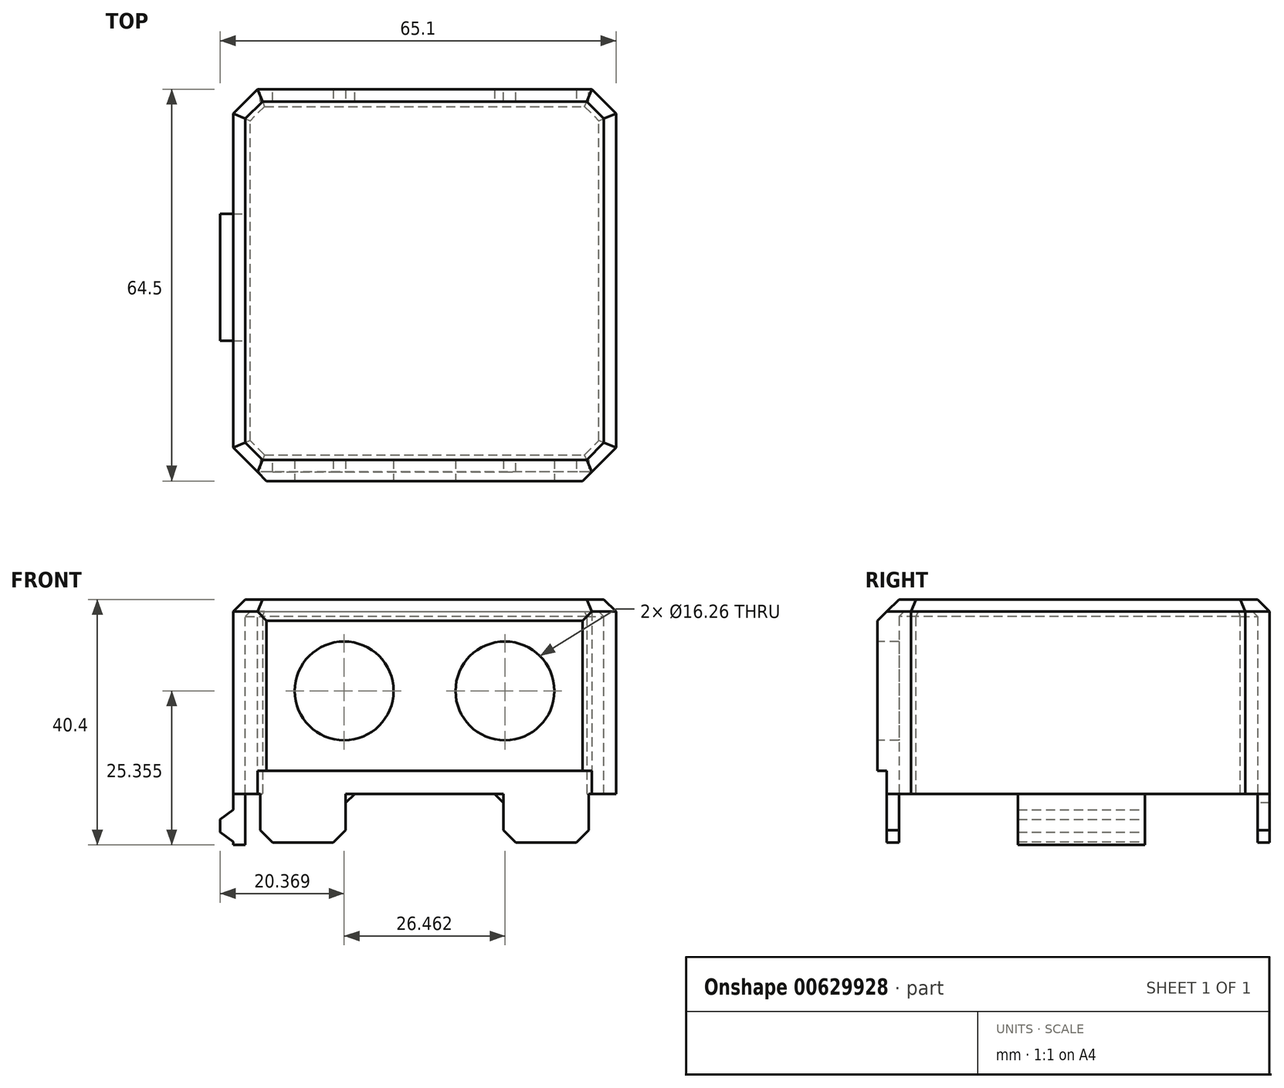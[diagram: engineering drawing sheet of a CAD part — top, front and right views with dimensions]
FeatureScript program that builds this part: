
annotation { "Feature Type Name" : "Feature", "Feature Type Description" : "" }
export const myFeature = defineFeature(function(context is Context, id is Id, definition is map)
    precondition{}
    {
        {
            var Q0;
            Q0=qCreatedBy(makeId("Top.planeOp"),FACE);
            var sketch = newSketch(context, id + "F0", { "sketchPlane" : qUnion([Q0])});
            skLineSegment(sketch, "E0.bottom", {"start": v(0, 0) * mm, "end": v(63, 0) * mm});
            skLineSegment(sketch, "E0.top", {"start": v(0, 63) * mm, "end": v(63, 63) * mm});
            skLineSegment(sketch, "E0.left", {"start": v(0, 0) * mm, "end": v(0, 63) * mm});
            skLineSegment(sketch, "E0.right", {"start": v(63, 0) * mm, "end": v(63, 63) * mm});
            skSolve(sketch);
        }
        {
            var Q0;
            Q0=makeQuery(id+"F0.imprint","IMPRINT",FACE,{"disambiguationData":[TD([[makeQuery(id+"F0.imprint","IMPRINT",EDGE,{"derivedFrom":sQuery(id+"F0.wireOp",EDGE,"E0.bottom")}),1.0]])]});
            extrude(context, id + "F1", {"entities" : qUnion([Q0]), "depth" : 32 * mm, "offsetDistance" : 25 * mm});
        }
        {
            var Q0;
            Q0=makeQuery(id+"F1.opExtrude","SWEPT_EDGE",EDGE,{"disambiguationData":[OSD([sQuery(id+"F0.wireOp",EDGE,"E0.bottom"),sQuery(id+"F0.wireOp",EDGE,"E0.right")])]});
            var Q1;
            Q1=makeQuery(id+"F1.opExtrude","SWEPT_EDGE",EDGE,{"disambiguationData":[OSD([sQuery(id+"F0.wireOp",EDGE,"E0.top"),sQuery(id+"F0.wireOp",EDGE,"E0.right")])]});
            var Q2;
            Q2=makeQuery(id+"F1.opExtrude","SWEPT_EDGE",EDGE,{"disambiguationData":[OSD([sQuery(id+"F0.wireOp",EDGE,"E0.bottom"),sQuery(id+"F0.wireOp",EDGE,"E0.left")])]});
            var Q3;
            Q3=makeQuery(id+"F1.opExtrude","SWEPT_EDGE",EDGE,{"disambiguationData":[OSD([sQuery(id+"F0.wireOp",EDGE,"E0.top"),sQuery(id+"F0.wireOp",EDGE,"E0.left")])]});
            chamfer(context, id + "F2", {"entities" : qUnion([Q0, Q1, Q2, Q3]), "width" : 4 * mm, "tangentPropagation" : true});
        }
        {
            var Q0;
            Q0=makeQuery(id+"F1.opExtrude","CAP_FACE",FACE,{"disambiguationData":[OSD([sQuery(id+"F0.wireOp",EDGE,"E0.bottom"),sQuery(id+"F0.wireOp",EDGE,"E0.top"),sQuery(id+"F0.wireOp",EDGE,"E0.left"),sQuery(id+"F0.wireOp",EDGE,"E0.right")])],"isStart":false});
            chamfer(context, id + "F3", {"entities" : qUnion([Q0]), "width" : 2 * mm, "tangentPropagation" : true});
        }
        {
            var Q0;
            Q0=makeQuery(id+"F1.opExtrude","CAP_FACE",FACE,{"disambiguationData":[OSD([sQuery(id+"F0.wireOp",EDGE,"E0.bottom"),sQuery(id+"F0.wireOp",EDGE,"E0.top"),sQuery(id+"F0.wireOp",EDGE,"E0.left"),sQuery(id+"F0.wireOp",EDGE,"E0.right")])],"isStart":true});
            shell(context, id + "F4", {"entities" : qUnion([Q0]), "thickness" : 2 * mm});
        }
        {
            var Q0;
            Q0=makeQuery(id+"F1.opExtrude","SWEPT_FACE",FACE,{"disambiguationData":[OSD([sQuery(id+"F0.wireOp",EDGE,"E0.bottom")])]});
            var sketch = newSketch(context, id + "F5", { "sketchPlane" : qUnion([Q0])});
            skLineSegment(sketch, "E1.bottom", {"start": v(59, 30) * mm, "end": v(4, 30) * mm});
            skLineSegment(sketch, "E1.top", {"start": v(59, 3.8) * mm, "end": v(4, 3.8) * mm});
            skLineSegment(sketch, "E1.left", {"start": v(59, 30) * mm, "end": v(59, 3.8) * mm});
            skLineSegment(sketch, "E1.right", {"start": v(4, 30) * mm, "end": v(4, 3.8) * mm});
            skSolve(sketch);
        }
        {
            var Q0;
            Q0=makeQuery(id+"F5.imprint","IMPRINT",FACE,{"disambiguationData":[TD([[makeQuery(id+"F5.imprint","IMPRINT",EDGE,{"derivedFrom":sQuery(id+"F5.wireOp",EDGE,"E1.bottom")}),1.0]])]});
            extrude(context, id + "F6", {"entities" : qUnion([Q0]), "operationType" : NewBodyOperationType.ADD, "depth" : 1.5 * mm, "offsetDistance" : 25 * mm});
        }
        {
            var Q0;
            Q0=makeQuery(id+"F6.opExtrude","CAP_EDGE",EDGE,{"disambiguationData":[OSD([sQuery(id+"F5.wireOp",EDGE,"E1.bottom")])],"isStart":false});
            var Q1;
            Q1=makeQuery(id+"F6.opExtrude","CAP_EDGE",EDGE,{"disambiguationData":[OSD([sQuery(id+"F5.wireOp",EDGE,"E1.right")])],"isStart":false});
            var Q2;
            Q2=makeQuery(id+"F6.opExtrude","CAP_EDGE",EDGE,{"disambiguationData":[OSD([sQuery(id+"F5.wireOp",EDGE,"E1.left")])],"isStart":false});
            chamfer(context, id + "F7", {"entities" : qUnion([Q0, Q1, Q2]), "width" : 1.5 * mm, "tangentPropagation" : true});
        }
        {
            var Q0;
            Q0=makeQuery(id+"F6.opExtrude","CAP_FACE",FACE,{"disambiguationData":[OSD([sQuery(id+"F5.wireOp",EDGE,"E1.bottom"),sQuery(id+"F5.wireOp",EDGE,"E1.top"),sQuery(id+"F5.wireOp",EDGE,"E1.left"),sQuery(id+"F5.wireOp",EDGE,"E1.right")])],"isStart":false});
            var sketch = newSketch(context, id + "F8", { "sketchPlane" : qUnion([Q0])});
            skCircle(sketch, "E2", {"center": v(18.27, 16.95) * mm, "radius": 8.13 * mm});
            skCircle(sketch, "E3", {"center": v(44.73, 16.95) * mm, "radius": 8.13 * mm});
            skSolve(sketch);
        }
        {
            var Q0;
            Q0=makeQuery(id+"F8.imprint","IMPRINT",FACE,{"disambiguationData":[TD([[makeQuery(id+"F8.imprint","IMPRINT",EDGE,{"derivedFrom":sQuery(id+"F8.wireOp",EDGE,"E2")}),1.0]])]});
            var Q1;
            Q1=makeQuery(id+"F8.imprint","IMPRINT",FACE,{"disambiguationData":[TD([[makeQuery(id+"F8.imprint","IMPRINT",EDGE,{"derivedFrom":sQuery(id+"F8.wireOp",EDGE,"E3")}),1.0]])]});
            var Q2;
            {var subQ0=sQuery(id+"F0.wireOp",EDGE,"E0.bottom");Q2=makeQuery(id+"F4.opShell","OFFSET_FACE",FACE,{"disambiguationData":[OSD([subQ0]),TDD([makeQuery(id+"F1.opExtrude","SWEPT_FACE",FACE,{"disambiguationData":[OSD([subQ0])]})])]});}
            extrude(context, id + "F9", {"entities" : qUnion([Q0, Q1]), "operationType" : NewBodyOperationType.REMOVE, "endBound" : BoundingType.UP_TO_SURFACE, "oppositeDirection" : true, "depth" : 25 * mm, "endBoundEntityFace" : qUnion([Q2]), "offsetDistance" : 25 * mm});
        }
        {
            var Q0;
            Q0=makeQuery(id+"F1.opExtrude","SWEPT_FACE",FACE,{"disambiguationData":[OSD([sQuery(id+"F0.wireOp",EDGE,"E0.bottom")])]});
            var sketch = newSketch(context, id + "F10", { "sketchPlane" : qUnion([Q0])});
            skLineSegment(sketch, "E4.bottom", {"start": v(4.5, 0) * mm, "end": v(18.5, 0) * mm});
            skLineSegment(sketch, "E4.top", {"start": v(4.5, -8) * mm, "end": v(18.5, -8) * mm});
            skLineSegment(sketch, "E4.left", {"start": v(4.5, 0) * mm, "end": v(4.5, -8) * mm});
            skLineSegment(sketch, "E4.right", {"start": v(18.5, 0) * mm, "end": v(18.5, -8) * mm});
            skLineSegment(sketch, "E5.bottom", {"start": v(58.5, 0) * mm, "end": v(44.5, 0) * mm});
            skLineSegment(sketch, "E5.top", {"start": v(58.5, -8) * mm, "end": v(44.5, -8) * mm});
            skLineSegment(sketch, "E5.left", {"start": v(58.5, 0) * mm, "end": v(58.5, -8) * mm});
            skLineSegment(sketch, "E5.right", {"start": v(44.5, 0) * mm, "end": v(44.5, -8) * mm});
            skSolve(sketch);
        }
        {
            var Q0;
            Q0=makeQuery(id+"F10.imprint","IMPRINT",FACE,{"disambiguationData":[TD([[makeQuery(id+"F10.imprint","IMPRINT",EDGE,{"derivedFrom":sQuery(id+"F10.wireOp",EDGE,"E4.bottom")}),-1.0]])]});
            var Q1;
            Q1=makeQuery(id+"F10.imprint","IMPRINT",FACE,{"disambiguationData":[TD([[makeQuery(id+"F10.imprint","IMPRINT",EDGE,{"derivedFrom":sQuery(id+"F10.wireOp",EDGE,"E5.bottom")}),-1.0]])]});
            var Q2;
            {var subQ0=sQuery(id+"F0.wireOp",EDGE,"E0.bottom");Q2=makeQuery(id+"F4.opShell","OFFSET_FACE",FACE,{"disambiguationData":[OSD([subQ0]),TDD([makeQuery(id+"F1.opExtrude","SWEPT_FACE",FACE,{"disambiguationData":[OSD([subQ0])]})])]});}
            extrude(context, id + "F11", {"entities" : qUnion([Q0, Q1]), "operationType" : NewBodyOperationType.ADD, "endBound" : BoundingType.UP_TO_SURFACE, "oppositeDirection" : true, "depth" : 25 * mm, "endBoundEntityFace" : qUnion([Q2]), "offsetDistance" : 25 * mm});
        }
        {
            var Q0;
            Q0=makeQuery(id+"F1.opExtrude","SWEPT_FACE",FACE,{"disambiguationData":[OSD([sQuery(id+"F0.wireOp",EDGE,"E0.top")])]});
            var Q1;
            Q1=makeQuery(id+"F11.boolean.opBoolean","MERGE",FACE,{"derivedFrom":[makeQuery(id+"F1.opExtrude","SWEPT_FACE",FACE,{"disambiguationData":[OSD([sQuery(id+"F0.wireOp",EDGE,"E0.bottom")])]}),makeQuery(id+"F11.opExtrude","CAP_FACE",FACE,{"disambiguationData":[OSD([sQuery(id+"F10.wireOp",EDGE,"E4.bottom"),sQuery(id+"F10.wireOp",EDGE,"E4.top"),sQuery(id+"F10.wireOp",EDGE,"E4.left"),sQuery(id+"F10.wireOp",EDGE,"E4.right")])],"isStart":true})]});
            cPlane(context, id + "F12", {"entities" : qUnion([Q0, Q1]), "cplaneType" : CPlaneType.MID_PLANE, "offset" : 25 * mm, "width" : 150 * mm, "height" : 150 * mm});
        }
        {
            var Q0;
            Q0=makeQuery(id+"F1.opExtrude","SWEPT_FACE",FACE,{"disambiguationData":[OSD([sQuery(id+"F0.wireOp",EDGE,"E0.top")])]});
            var sketch = newSketch(context, id + "F13", { "sketchPlane" : qUnion([Q0])});
            skLineSegment(sketch, "E6.bottom", {"start": v(-4.5, 0) * mm, "end": v(-18.5, 0) * mm});
            skLineSegment(sketch, "E6.top", {"start": v(-4.5, -8) * mm, "end": v(-18.5, -8) * mm});
            skLineSegment(sketch, "E6.left", {"start": v(-4.5, 0) * mm, "end": v(-4.5, -8) * mm});
            skLineSegment(sketch, "E6.right", {"start": v(-18.5, 0) * mm, "end": v(-18.5, -8) * mm});
            skLineSegment(sketch, "E7.bottom", {"start": v(-58.5, 0) * mm, "end": v(-44.5, 0) * mm});
            skLineSegment(sketch, "E7.top", {"start": v(-58.5, -8) * mm, "end": v(-44.5, -8) * mm});
            skLineSegment(sketch, "E7.left", {"start": v(-58.5, 0) * mm, "end": v(-58.5, -8) * mm});
            skLineSegment(sketch, "E7.right", {"start": v(-44.5, 0) * mm, "end": v(-44.5, -8) * mm});
            skSolve(sketch);
        }
        {
            var Q0;
            Q0=makeQuery(id+"F13.imprint","IMPRINT",FACE,{"disambiguationData":[TD([[makeQuery(id+"F13.imprint","IMPRINT",EDGE,{"derivedFrom":sQuery(id+"F13.wireOp",EDGE,"E7.bottom")}),1.0]])]});
            var Q1;
            Q1=makeQuery(id+"F13.imprint","IMPRINT",FACE,{"disambiguationData":[TD([[makeQuery(id+"F13.imprint","IMPRINT",EDGE,{"derivedFrom":sQuery(id+"F13.wireOp",EDGE,"E6.bottom")}),1.0]])]});
            extrude(context, id + "F14", {"entities" : qUnion([Q0, Q1]), "operationType" : NewBodyOperationType.ADD, "oppositeDirection" : true, "depth" : 2 * mm, "offsetDistance" : 25 * mm});
        }
        {
            var Q0;
            Q0=makeQuery(id+"F11.opExtrude","SWEPT_EDGE",EDGE,{"disambiguationData":[OSD([sQuery(id+"F10.wireOp",EDGE,"E4.top"),sQuery(id+"F10.wireOp",EDGE,"E4.left")])]});
            var Q1;
            Q1=makeQuery(id+"F11.opExtrude","SWEPT_EDGE",EDGE,{"disambiguationData":[OSD([sQuery(id+"F10.wireOp",EDGE,"E4.top"),sQuery(id+"F10.wireOp",EDGE,"E4.right")])]});
            var Q2;
            Q2=makeQuery(id+"F11.opExtrude","SWEPT_EDGE",EDGE,{"disambiguationData":[OSD([sQuery(id+"F10.wireOp",EDGE,"E5.top"),sQuery(id+"F10.wireOp",EDGE,"E5.right")])]});
            var Q3;
            Q3=makeQuery(id+"F11.opExtrude","SWEPT_EDGE",EDGE,{"disambiguationData":[OSD([sQuery(id+"F10.wireOp",EDGE,"E5.top"),sQuery(id+"F10.wireOp",EDGE,"E5.left")])]});
            var Q4;
            Q4=makeQuery(id+"F14.opExtrude","SWEPT_EDGE",EDGE,{"disambiguationData":[OSD([sQuery(id+"F13.wireOp",EDGE,"E6.top"),sQuery(id+"F13.wireOp",EDGE,"E6.right")])]});
            var Q5;
            Q5=makeQuery(id+"F14.opExtrude","SWEPT_EDGE",EDGE,{"disambiguationData":[OSD([sQuery(id+"F13.wireOp",EDGE,"E6.top"),sQuery(id+"F13.wireOp",EDGE,"E6.left")])]});
            var Q6;
            Q6=makeQuery(id+"F14.opExtrude","SWEPT_EDGE",EDGE,{"disambiguationData":[OSD([sQuery(id+"F13.wireOp",EDGE,"E7.top"),sQuery(id+"F13.wireOp",EDGE,"E7.left")])]});
            var Q7;
            Q7=makeQuery(id+"F14.opExtrude","SWEPT_EDGE",EDGE,{"disambiguationData":[OSD([sQuery(id+"F13.wireOp",EDGE,"E7.top"),sQuery(id+"F13.wireOp",EDGE,"E7.right")])]});
            chamfer(context, id + "F15", {"entities" : qUnion([Q0, Q1, Q2, Q3, Q4, Q5, Q6, Q7]), "width" : 2 * mm, "tangentPropagation" : true});
        }
        {
            var Q0;
            Q0=makeQuery(id+"F14.opExtrude","SWEPT_EDGE",EDGE,{"disambiguationData":[OSD([sQuery(id+"F0.wireOp",EDGE,"E0.top"),sQuery(id+"F13.wireOp",EDGE,"E6.bottom"),sQuery(id+"F13.wireOp",EDGE,"E6.right")])]});
            var Q1;
            Q1=makeQuery(id+"F11.opExtrude","SWEPT_EDGE",EDGE,{"disambiguationData":[OSD([sQuery(id+"F0.wireOp",EDGE,"E0.bottom"),sQuery(id+"F10.wireOp",EDGE,"E4.bottom"),sQuery(id+"F10.wireOp",EDGE,"E4.right")])]});
            var Q2;
            Q2=makeQuery(id+"F11.opExtrude","SWEPT_EDGE",EDGE,{"disambiguationData":[OSD([sQuery(id+"F0.wireOp",EDGE,"E0.bottom"),sQuery(id+"F10.wireOp",EDGE,"E5.bottom"),sQuery(id+"F10.wireOp",EDGE,"E5.right")])]});
            var Q3;
            Q3=makeQuery(id+"F14.opExtrude","SWEPT_EDGE",EDGE,{"disambiguationData":[OSD([sQuery(id+"F0.wireOp",EDGE,"E0.top"),sQuery(id+"F13.wireOp",EDGE,"E7.bottom"),sQuery(id+"F13.wireOp",EDGE,"E7.right")])]});
            chamfer(context, id + "F16", {"entities" : qUnion([Q0, Q1, Q2, Q3]), "width" : 1.5 * mm, "tangentPropagation" : true});
        }
        {
            var Q0;
            Q0=qCreatedBy(id+"F12.planeOp",FACE);
            var sketch = newSketch(context, id + "F17", { "sketchPlane" : qUnion([Q0])});
            skLineSegment(sketch, "E8.bottom", {"start": v(0, 0) * mm, "end": v(-2, 0) * mm});
            skLineSegment(sketch, "E8.top", {"start": v(0, -8.4) * mm, "end": v(-2, -8.4) * mm});
            skLineSegment(sketch, "E8.left", {"start": v(0, 0) * mm, "end": v(0, -8.4) * mm});
            skLineSegment(sketch, "E8.right", {"start": v(-2, 0) * mm, "end": v(-2, -8.4) * mm});
            skLineSegment(sketch, "E9", {"start": v(0, -7.9) * mm, "end": v(2.1, -6.3) * mm});
            skLineSegment(sketch, "E10", {"start": v(2.1, -6.3) * mm, "end": v(2.1, -4.2) * mm});
            skLineSegment(sketch, "E11", {"start": v(2.1, -4.2) * mm, "end": v(0, -2.6) * mm});
            skLineSegment(sketch, "E12", {"start": v(0, -2.6) * mm, "end": v(0, -7.9) * mm});
            skSolve(sketch);
        }
        {
            var Q0;
            {var subQ3=sQuery(id+"F17.wireOp",EDGE,"E8.bottom");Q0=makeQuery(id+"F17.imprint","IMPRINT",FACE,{"disambiguationData":[TD([[makeQuery(id+"F17.imprint","IMPRINT",EDGE,{"derivedFrom":subQ3}),1.0]])]});}
            var Q1;
            Q1=makeQuery(id+"F17.imprint","IMPRINT",FACE,{"disambiguationData":[TD([[makeQuery(id+"F17.imprint","IMPRINT",EDGE,{"derivedFrom":sQuery(id+"F17.wireOp",EDGE,"E9")}),1.0]])]});
            extrude(context, id + "F18", {"entities" : qUnion([Q0, Q1]), "operationType" : NewBodyOperationType.ADD, "oppositeDirection" : true, "depth" : 9.9 * mm, "offsetDistance" : 25 * mm});
        }
        {
            var Q0;
            Q0=makeQuery(id+"F18.opExtrude","CAP_FACE",FACE,{"disambiguationData":[OSD([sQuery(id+"F17.wireOp",EDGE,"E8.bottom"),sQuery(id+"F17.wireOp",EDGE,"E8.top"),sQuery(id+"F17.wireOp",EDGE,"E8.left"),sQuery(id+"F17.wireOp",EDGE,"E8.right"),sQuery(id+"F17.wireOp",EDGE,"E9"),sQuery(id+"F17.wireOp",EDGE,"E10"),sQuery(id+"F17.wireOp",EDGE,"E11")])],"isStart":true});
            extrude(context, id + "F19", {"entities" : qUnion([Q0]), "operationType" : NewBodyOperationType.ADD, "depth" : 11 * mm, "offsetDistance" : 25 * mm});
        }
        {
            var Q0;
            {var subQ0=sQuery(id+"F17.wireOp",EDGE,"E8.left");var subQ1=makeQuery(id+"F17.imprint","IMPRINT",EDGE,{"disambiguationData":[TD([[makeQuery(id+"F17.imprint","INTERSECT",VERTEX,{"derivedFrom":[sQuery(id+"F17.wireOp",EDGE,"E8.bottom"),subQ0]}),-1.0]])],"derivedFrom":subQ0});Q0=makeQuery(id+"F19.boolean.opBoolean","MERGE",FACE,{"derivedFrom":[makeQuery(id+"F18.boolean.opBoolean","MERGE",FACE,{"derivedFrom":[makeQuery(id+"F1.opExtrude","SWEPT_FACE",FACE,{"disambiguationData":[OSD([sQuery(id+"F0.wireOp",EDGE,"E0.left")])]}),makeQuery(id+"F18.opExtrude","SWEPT_FACE",FACE,{"disambiguationData":[OSD([subQ0]),TDD([subQ1])]})]}),makeQuery(id+"F19.opExtrude","SWEPT_FACE",FACE,{"disambiguationData":[OSD([subQ0]),TDD([makeQuery(id+"F18.opExtrude","CAP_EDGE",EDGE,{"disambiguationData":[OSD([subQ0]),TDD([subQ1])],"isStart":true})])]})]});}
            var Q1;
            Q1=makeQuery(id+"F1.opExtrude","SWEPT_FACE",FACE,{"disambiguationData":[OSD([sQuery(id+"F0.wireOp",EDGE,"E0.right")])]});
            cPlane(context, id + "F20", {"entities" : qUnion([Q0, Q1]), "cplaneType" : CPlaneType.MID_PLANE, "offset" : 25 * mm, "width" : 150 * mm, "height" : 150 * mm});
        }
    });
